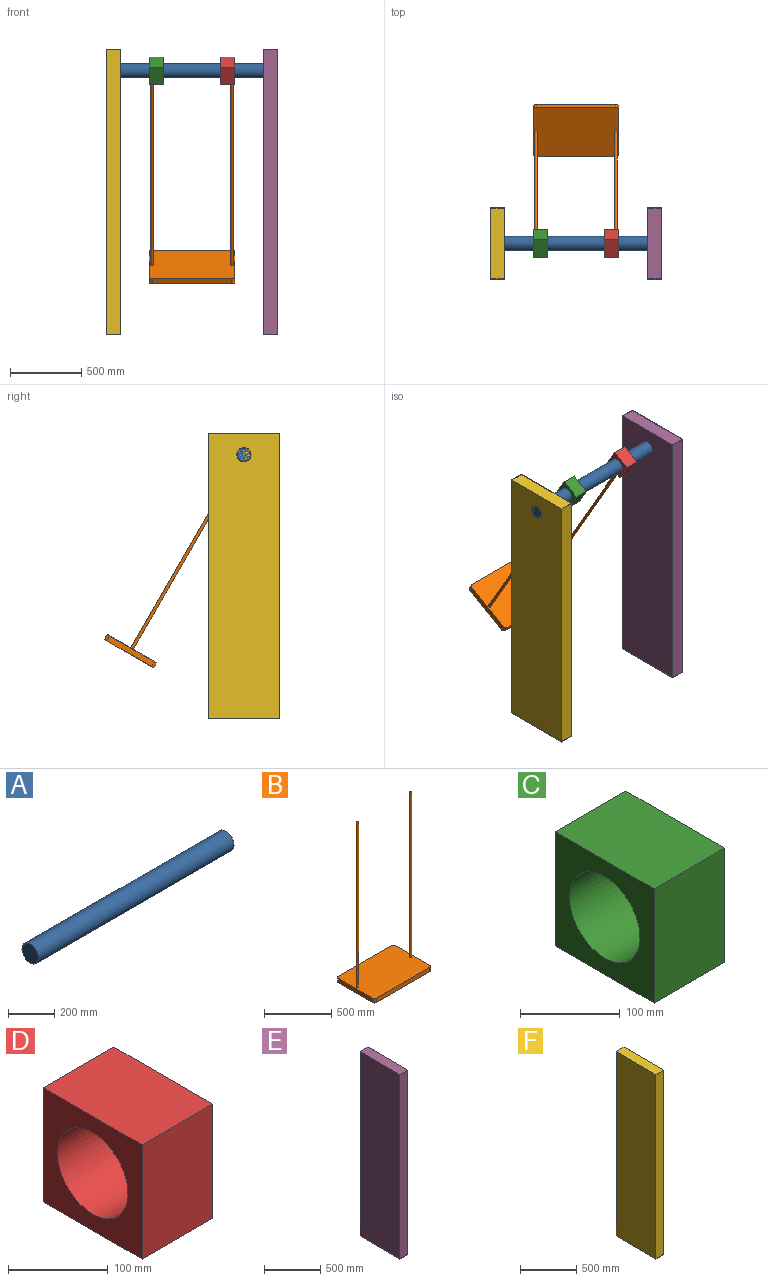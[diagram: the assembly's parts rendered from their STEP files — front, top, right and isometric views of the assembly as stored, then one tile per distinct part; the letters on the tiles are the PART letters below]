
ASSEMBLY  parts=6 mates=6
PART A: 6 faces, bbox 1200x100x100 mm
  f0: cylinder r=50mm len=1200mm, axis (-1,0,0), area 376991.1mm2, adj f1,f2
  f1: plane 100x100mm, normal (1,0,0), area 7854mm2, adj f0
  f2: plane 100x100mm, normal (-1,0,0), area 7854mm2, adj f0
  f3: cylinder r=47.5mm len=1195mm, axis (-1,0,0), area 356649.3mm2, adj f4,f5
  f4: plane 95x95mm, normal (-1,0,0), area 7088.2mm2, adj f3
  f5: plane 95x95mm, normal (1,0,0), area 7088.2mm2, adj f3
PART B: 14 faces, bbox 600x400x1540 mm
  f0: plane 560x40mm, normal (0,1,0), area 22400mm2, adj f1,f7,f8,f9
  f1: cylinder r=20mm len=40mm, axis (0,0,-1), area 1256.6mm2, adj f0,f2,f8,f9
  f2: plane 360x40mm, normal (-1,0,0), area 14400mm2, adj f1,f3,f8,f9
  f3: cylinder r=20mm len=40mm, axis (0,0,-1), area 1256.6mm2, adj f2,f4,f8,f9
  f4: plane 560x40mm, normal (0,-1,0), area 22400mm2, adj f3,f5,f8,f9
  f5: cylinder r=20mm len=40mm, axis (0,0,-1), area 1256.6mm2, adj f4,f6,f8,f9
  f6: plane 360x40mm, normal (1,0,0), area 14400mm2, adj f5,f7,f8,f9
  f7: cylinder r=20mm len=40mm, axis (0,0,-1), area 1256.6mm2, adj f0,f6,f8,f9
  f8: plane 600x400mm, normal (0,0,1), area 239028.3mm2, adj f0,f1,f2,f3,f4,f5,f6,f7
  f9: plane 600x400mm, normal (0,0,-1), area 239656.6mm2, adj f0,f1,f2,f3,f4,f5,f6,f7
  f10: cylinder r=10mm len=1500mm, axis (0,0,-1), area 94247.8mm2, adj f8,f11
  f11: plane 20x20mm, normal (0,0,1), area 314.2mm2, adj f10
  f12: cylinder r=10mm len=1500mm, axis (0,0,-1), area 94247.8mm2, adj f8,f13
  f13: plane 20x20mm, normal (0,0,1), area 314.2mm2, adj f12
PART C: 7 faces, bbox 100x140x140 mm
  f0: plane 140x100mm, normal (0,0,1), area 14000mm2, adj f1,f4,f5,f6
  f1: plane 140x100mm, normal (0,-1,0), area 14000mm2, adj f0,f2,f5,f6
  f2: plane 140x100mm, normal (0,0,-1), area 14000mm2, adj f1,f4,f5,f6
  f3: cylinder r=50mm len=100mm, axis (1,0,0), area 31415.9mm2, adj f5,f6
  f4: plane 140x100mm, normal (0,1,0), area 14000mm2, adj f0,f2,f5,f6
  f5: plane 140x140mm, normal (-1,0,0), area 11746mm2, adj f0,f1,f2,f3,f4
  f6: plane 140x140mm, normal (1,0,0), area 11746mm2, adj f0,f1,f2,f3,f4
PART D: 7 faces, bbox 100x140x140 mm
  f0: plane 140x100mm, normal (0,0,1), area 14000mm2, adj f1,f4,f5,f6
  f1: plane 140x100mm, normal (0,-1,0), area 14000mm2, adj f0,f2,f5,f6
  f2: plane 140x100mm, normal (0,0,-1), area 14000mm2, adj f1,f4,f5,f6
  f3: cylinder r=50mm len=100mm, axis (-1,0,0), area 31415.9mm2, adj f5,f6
  f4: plane 140x100mm, normal (0,1,0), area 14000mm2, adj f0,f2,f5,f6
  f5: plane 140x140mm, normal (1,0,0), area 11746mm2, adj f0,f1,f2,f3,f4
  f6: plane 140x140mm, normal (-1,0,0), area 11746mm2, adj f0,f1,f2,f3,f4
PART E: 12 faces, bbox 100x500x2000 mm
  f0: plane 2000x100mm, normal (0,1,0), area 200000mm2, adj f1,f3,f4,f5
  f1: plane 500x100mm, normal (0,0,1), area 50000mm2, adj f0,f2,f4,f5
  f2: plane 2000x100mm, normal (0,-1,0), area 200000mm2, adj f1,f3,f4,f5
  f3: plane 500x100mm, normal (0,0,-1), area 50000mm2, adj f0,f2,f4,f5
  f4: plane 2000x500mm, normal (1,0,0), area 1000000mm2, adj f0,f1,f2,f3
  f5: plane 2000x500mm, normal (-1,0,0), area 1000000mm2, adj f0,f1,f2,f3
  f6: plane 1995x95mm, normal (0,-1,0), area 189525mm2, adj f7,f9,f10,f11
  f7: plane 495x95mm, normal (0,0,-1), area 47025mm2, adj f6,f8,f10,f11
  f8: plane 1995x95mm, normal (0,1,0), area 189525mm2, adj f7,f9,f10,f11
  f9: plane 495x95mm, normal (0,0,1), area 47025mm2, adj f6,f8,f10,f11
  f10: plane 1995x495mm, normal (-1,0,0), area 987525mm2, adj f6,f7,f8,f9
  f11: plane 1995x495mm, normal (1,0,0), area 987525mm2, adj f6,f7,f8,f9
PART F: 12 faces, bbox 100x500x2000 mm
  f0: plane 2000x100mm, normal (0,1,0), area 200000mm2, adj f1,f3,f4,f5
  f1: plane 500x100mm, normal (0,0,1), area 50000mm2, adj f0,f2,f4,f5
  f2: plane 2000x100mm, normal (0,-1,0), area 200000mm2, adj f1,f3,f4,f5
  f3: plane 500x100mm, normal (0,0,-1), area 50000mm2, adj f0,f2,f4,f5
  f4: plane 2000x500mm, normal (-1,0,0), area 1000000mm2, adj f0,f1,f2,f3
  f5: plane 2000x500mm, normal (1,0,0), area 1000000mm2, adj f0,f1,f2,f3
  f6: plane 1995x95mm, normal (0,-1,0), area 189525mm2, adj f7,f9,f10,f11
  f7: plane 495x95mm, normal (0,0,-1), area 47025mm2, adj f6,f8,f10,f11
  f8: plane 1995x95mm, normal (0,1,0), area 189525mm2, adj f7,f9,f10,f11
  f9: plane 495x95mm, normal (0,0,1), area 47025mm2, adj f6,f8,f10,f11
  f10: plane 1995x495mm, normal (1,0,0), area 987525mm2, adj f6,f7,f8,f9
  f11: plane 1995x495mm, normal (-1,0,0), area 987525mm2, adj f6,f7,f8,f9
PLACE A t=(-134.88,-116.57,-58.05)mm fixed
PLACE B rot(axis=(1,0,0),30deg) t=(-134.88,688.43,-602.35)mm
PLACE C rot(axis=(-1,0,0),60deg) t=(-84.88,-852.69,366.95)mm
PLACE D rot(axis=(1,0,0),120deg) t=(-184.88,619.55,1216.95)mm
PLACE E t=(-134.88,-116.57,-58.05)mm
PLACE F t=(-134.88,-116.57,-58.05)mm
MATE revolute A.f0 <-> D.f3  axis (1,0,0) through (465.12,-116.57,791.95)mm
MATE fastened F.f4 <-> A.f2  axis (-1,0,0) through (-734.88,-116.57,-58.05)mm
MATE fastened B.f10 <-> C.f4  axis (0,-0.5,0.87) through (-414.88,-81.57,731.33)mm
MATE fastened D.f1 <-> B.f13  axis (0,0.5,-0.87) through (115.12,-81.57,731.33)mm
MATE revolute A.f0 <-> C.f3  axis (-1,0,0) through (-734.88,-116.57,791.95)mm
MATE fastened E.f4 <-> A.f1  axis (1,0,0) through (465.12,-116.57,-58.05)mm
